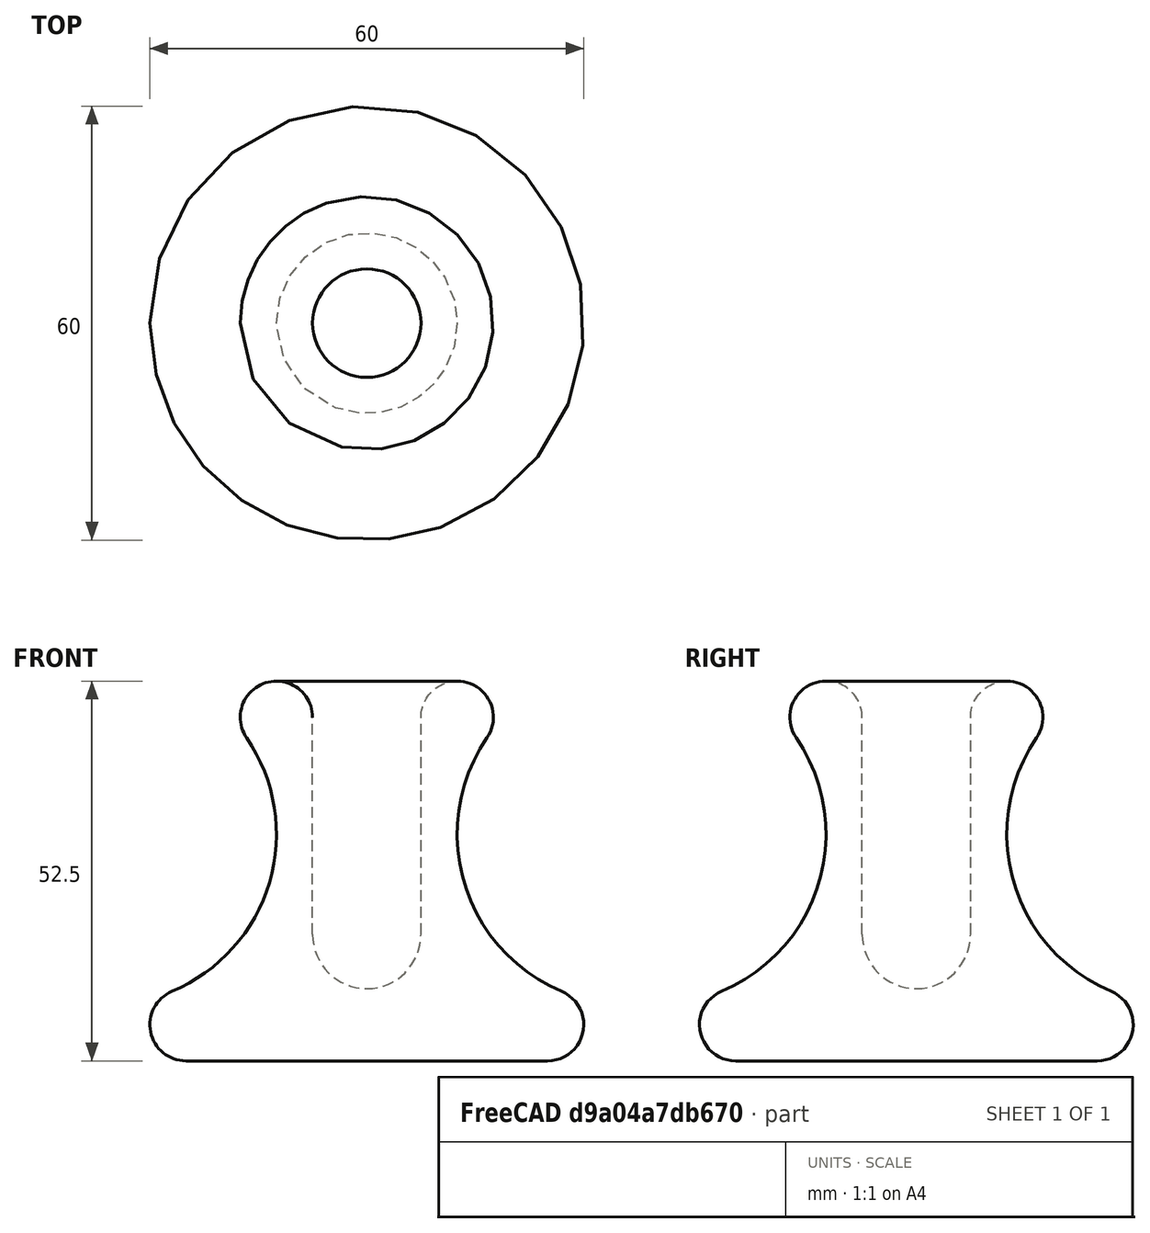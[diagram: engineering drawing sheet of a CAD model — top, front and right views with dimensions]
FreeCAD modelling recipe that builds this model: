
FCSTD DOCUMENT  (FreeCAD 0.16RUnknown)
Label: inkwell
License: All rights reserved
LicenseURL: http://en.wikipedia.org/wiki/All_rights_reserved
objects: Sketcher::SketchObject×1, PartDesign::Revolution×1, Mesh::Feature×1
note: 3 computed .brp shape members not serialized (recipe doc carries the construction recipe); baked Part::Feature solids carry a one-line shape summary decoded from their .brp

FEATURE [Sketcher::SketchObject] Sketch
  Placement = pos=(0,0,0) rot=(-1,0,0;4.71239rad)
  sketch-geometry (8):
    g0: LineSegment StartX=-25 StartY=0 StartZ=0 EndX=0 EndY=0 EndZ=0
    g1: LineSegment StartX=0 StartY=0 StartZ=0 EndX=0 EndY=10 EndZ=0
    g2: ArcOfCircle CenterX=0 CenterY=17.5 CenterZ=0 NormalX=0 NormalY=0 NormalZ=1 Radius=7.5 StartAngle=3.14159 EndAngle=4.71239
    g3: LineSegment StartX=-7.5 StartY=17.5 StartZ=0 EndX=-7.5 EndY=47.5 EndZ=0
    g4: ArcOfCircle CenterX=-36.086 CenterY=31.3488 CenterZ=0 NormalX=0 NormalY=0 NormalZ=1 Radius=23.586 StartAngle=5.11065 EndAngle=6.88362
    g5: ArcOfCircle CenterX=-12.5 CenterY=47.5 CenterZ=0 NormalX=0 NormalY=0 NormalZ=1 Radius=5 StartAngle=6.28319 EndAngle=10.0252
    g6: ArcOfCircle CenterX=-25 CenterY=5 CenterZ=0 NormalX=0 NormalY=0 NormalZ=1 Radius=5 StartAngle=1.96906 EndAngle=4.71239
    g7: LineSegment [constr] StartX=-12.5 StartY=47.5 StartZ=0 EndX=-12.5 EndY=0 EndZ=0
  constraints (27):
    c: PointOnObject(g0,g-1)
    c: Coincident(g0,g-1)
    c: Coincident(g1,g-1)
    c: PointOnObject(g1,g-2)
    c: PointOnObject(g2,g-2)
    c: Coincident(g2,g1)
    c: Coincident(g3,g2)
    c: Vertical(g3)
    c: Coincident(g5,g3)
    c: Tangent(g5,g3)
    c: Tangent(g2,g3)
    c: DistanceX(g2,g2) = 7.5
    c: Coincident(g6,g4)
    c: Coincident(g6,g0)
    c: Tangent(g6,g4)
    c: Tangent(g6,g0)
    c: DistanceX(g0,g0) = 25
    c: DistanceY(g3,g3) = 30
    c: DistanceY(g-1,g1) = 10
    c: DistanceY(g0,g6) = 5
    c: Coincident(g4,g5)
    c: Tangent(g4,g5)
    c: DistanceX(g5,g3) = 5
    c: Vertical(g7)
    c: Tangent(g7,g4)
    c: Coincident(g7,g5)
    c: PointOnObject(g7,g0)
FEATURE [PartDesign::Revolution] Revolution
  Angle = 360
  Axis = (0,0,1)
  Base = (0,0,0)
  Placement = pos=(0,0,0) rot=(-1,0,0;4.71239rad)
  ReferenceAxis = -> Sketch [V_Axis]
  Sketch = -> Sketch
FEATURE [Mesh::Feature] Mesh  label="Revolution (Meshed)"
